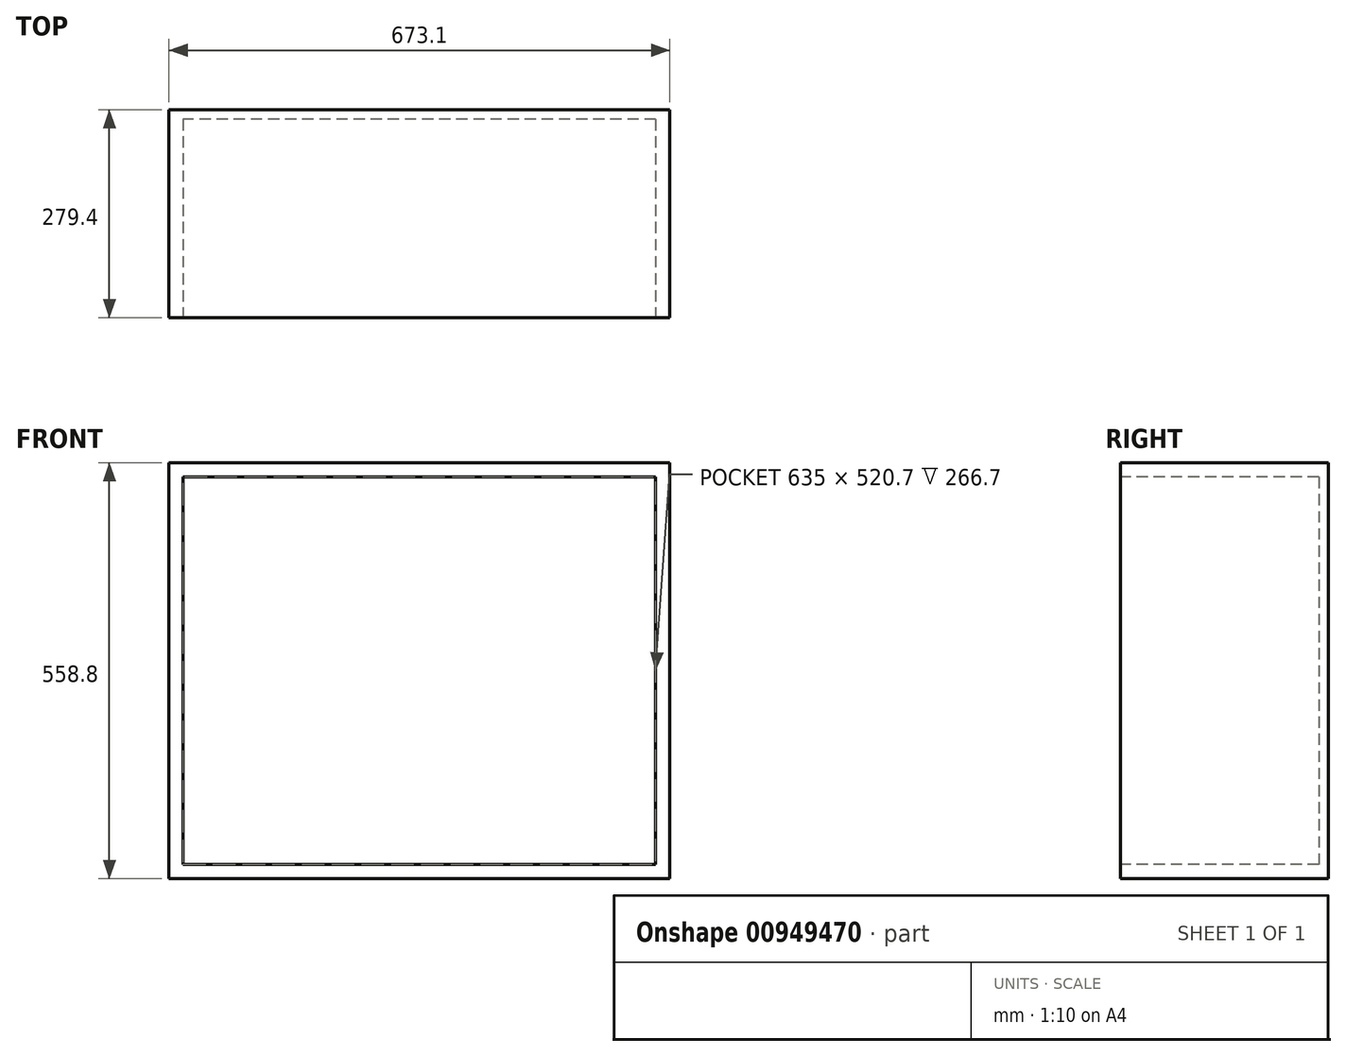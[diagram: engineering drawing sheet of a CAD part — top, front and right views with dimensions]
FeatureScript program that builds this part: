
annotation { "Feature Type Name" : "Feature", "Feature Type Description" : "" }
export const myFeature = defineFeature(function(context is Context, id is Id, definition is map)
    precondition{}
    {
        {
            var Q0;
            Q0=qCreatedBy(makeId("Front.planeOp"),FACE);
            var sketch = newSketch(context, id + "F0", { "sketchPlane" : qUnion([Q0])});
            skLineSegment(sketch, "E0.bottom", {"start": v(-336.55, 279.4) * mm, "end": v(336.55, 279.4) * mm});
            skLineSegment(sketch, "E0.top", {"start": v(-336.55, -279.4) * mm, "end": v(336.55, -279.4) * mm});
            skLineSegment(sketch, "E0.left", {"start": v(-336.55, 279.4) * mm, "end": v(-336.55, -279.4) * mm});
            skLineSegment(sketch, "E0.right", {"start": v(336.55, 279.4) * mm, "end": v(336.55, -279.4) * mm});
            skPoint(sketch, "E0.middle", {"position": v(0, 0) * mm});
            skSolve(sketch);
        }
        {
            var Q0;
            Q0=makeQuery(id+"F0.imprint","IMPRINT",FACE,{"disambiguationData":[TD([[makeQuery(id+"F0.imprint","IMPRINT",EDGE,{"derivedFrom":sQuery(id+"F0.wireOp",EDGE,"E0.bottom")}),-1.0]])]});
            extrude(context, id + "F1", {"entities" : qUnion([Q0]), "endBound" : BoundingType.SYMMETRIC, "depth" : 279.4 * mm});
        }
        {
            var Q0;
            Q0=makeQuery(id+"F1.opExtrude","CAP_FACE",FACE,{"disambiguationData":[OSD([sQuery(id+"F0.wireOp",EDGE,"E0.bottom"),sQuery(id+"F0.wireOp",EDGE,"E0.top"),sQuery(id+"F0.wireOp",EDGE,"E0.left"),sQuery(id+"F0.wireOp",EDGE,"E0.right")])],"isStart":false});
            var sketch = newSketch(context, id + "F2", { "sketchPlane" : qUnion([Q0])});
            skLineSegment(sketch, "E1.bottom", {"start": v(317.5, 260.35) * mm, "end": v(-317.5, 260.35) * mm});
            skLineSegment(sketch, "E1.top", {"start": v(317.5, -260.35) * mm, "end": v(-317.5, -260.35) * mm});
            skLineSegment(sketch, "E1.left", {"start": v(317.5, 260.35) * mm, "end": v(317.5, -260.35) * mm});
            skLineSegment(sketch, "E1.right", {"start": v(-317.5, 260.35) * mm, "end": v(-317.5, -260.35) * mm});
            skPoint(sketch, "E1.middle", {"position": v(0, 0) * mm});
            skSolve(sketch);
        }
        {
            var Q0;
            Q0=qSketchRegion(id+"F2",true);
            var Q1;
            Q1=makeQuery(id+"F1.opExtrude","CAP_FACE",FACE,{"disambiguationData":[OSD([sQuery(id+"F0.wireOp",EDGE,"E0.bottom"),sQuery(id+"F0.wireOp",EDGE,"E0.top"),sQuery(id+"F0.wireOp",EDGE,"E0.left"),sQuery(id+"F0.wireOp",EDGE,"E0.right")])],"isStart":true});
            extrude(context, id + "F3", {"entities" : qUnion([Q0]), "operationType" : NewBodyOperationType.REMOVE, "oppositeDirection" : true, "endBoundEntityFace" : qUnion([Q1]), "depth" : 266.7 * mm});
        }
        {
            var Q0;
            Q0=makeQuery(id+"F1.opExtrude","CAP_FACE",FACE,{"disambiguationData":[OSD([sQuery(id+"F0.wireOp",EDGE,"E0.bottom"),sQuery(id+"F0.wireOp",EDGE,"E0.top"),sQuery(id+"F0.wireOp",EDGE,"E0.left"),sQuery(id+"F0.wireOp",EDGE,"E0.right")])],"isStart":false});
            cPlane(context, id + "F4", {"entities" : qUnion([Q0]), "cplaneType" : CPlaneType.OFFSET, "offset" : .15 * mm, "width" : 150 * mm, "height" : 150 * mm});
        }
    });
